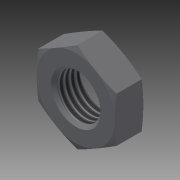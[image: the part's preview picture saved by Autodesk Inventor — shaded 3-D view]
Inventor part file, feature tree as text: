
AUTODESK INVENTOR PART (.ipt)
format: ipt  version: 2013 (Build 170138000, 138)  size: 150,016 bytes
history: native  units: in
note: dims shown in document units (in); Inventor stores cm internally (conversion verified against a paired STEP export)
features: other x70, sketch x3, revolve x2, extrude x1, thread x1
ambient origin geometry x8: Origin, YZ Plane, XZ Plane, XY Plane, X Axis, Y Axis, Z Axis, Center Point
bodies: Solid1 (feature_tree)
feature tree (77):
  sketch  "Sketch_8"  dims[d0=360.0deg d1=0.25in d2=0.0in]
  sketch  "Sketch_10"  dims[d3=360.0deg d4=0.1959in d5=0.0in]
  revolve  "Revolution1"  [1 undecoded]
  extrude  "Extrusion1"  Depth=0.1959in TaperAngle=0.0deg
  revolve  "Revolution2"  [1 undecoded]
  thread  "Thread1"  [1 undecoded]
  other  "NUT_XY"
  other  "NUT_YZ"
  other  "NUT_ZX"
  other  "NUT_X"
  other  "NUT_Y"
  other  "NUT_Z"
  other  "NUT_Center"
  other  "a1_XY"
  other  "a1_YZ"
  other  "a1_ZX"
  other  "a1_X"
  other  "a1_Y"
  other  "a1_Z"
  other  "a1_Center"
  other  "a2_XY"
  other  "a2_YZ"
  other  "a2_ZX"
  other  "a2_X"
  other  "a2_Y"
  other  "a2_Z"
  other  "a2_Center"
  other  "b1_XY"
  other  "b1_YZ"
  other  "b1_ZX"
  other  "b1_X"
  other  "b1_Y"
  other  "b1_Z"
  other  "b1_Center"
  other  "b2_XY"
  other  "b2_YZ"
  other  "b2_ZX"
  other  "b2_X"
  other  "b2_Y"
  other  "b2_Z"
  other  "b2_Center"
  other  "e_XY"
  other  "e_YZ"
  other  "e_ZX"
  other  "e_X"
  other  "e_Y"
  other  "e_Z"
  other  "e_Center"
  other  "th1_XY"
  other  "th1_YZ"
  other  "th1_ZX"
  other  "th1_X"
  other  "th1_Y"
  other  "th1_Z"
  other  "th1_Center"
  other  "th2_XY"
  other  "th2_YZ"
  other  "th2_ZX"
  other  "th2_X"
  other  "th2_Y"
  other  "th2_Z"
  other  "th2_Center"
  other  "ol1_XY"
  other  "ol1_YZ"
  other  "ol1_ZX"
  other  "ol1_X"
  other  "ol1_Y"
  other  "ol1_Z"
  other  "ol1_Center"
  other  "ol2_XY"
  other  "ol2_YZ"
  other  "ol2_ZX"
  other  "ol2_X"
  other  "ol2_Y"
  other  "ol2_Z"
  other  "ol2_Center"
  sketch  "Sketch_11"
note: 3 required parameter values undecoded (feature->parameter linkage not recoverable at this tier; creation-order binding heuristic only, values carry confidence <= 0.55)